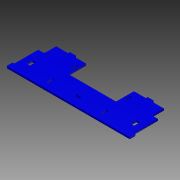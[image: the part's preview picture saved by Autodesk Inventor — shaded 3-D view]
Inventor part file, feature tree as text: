
AUTODESK INVENTOR PART (.ipt)
format: ipt  version: 2012 (Build 160160000, 160)  size: 176,640 bytes
history: native  units: mm
features: extrude x1, sketch x1
ambient origin geometry x8: Origin, YZ Plane, XZ Plane, XY Plane, X Axis, Y Axis, Z Axis, Center Point
feature tree (2):
  extrude  "Extrusion7"  Depth=30.0mm
  sketch  "Sketch1"  dims[d0=80.0mm d1=30.0mm d2=50.0mm d5=10.0mm d7=10.0mm d10=50.0mm d13=3.0mm d14=3.0mm d15=3.0mm d16=10.0mm d18=10.0mm d20=3.0mm d21=40.0mm d22=206.0mm d23=30.0mm d24=40.0mm d27=1.0mm d28=10.0mm d29=6.0mm d31=40.0mm d32=10.0mm d33=6.0mm d35=40.0mm d39=10.0mm d40=3.0mm d41=10.0mm d42=3.0mm d44=10.0mm d45=10.0mm d50=3.0mm d51=10.0mm d52=10.0mm d54=3.0mm d55=10.0mm d56=10.0mm d60=10.0mm d61=3.0mm d62=17.0mm d66=40.0mm d67=40.0mm d71=3.5mm d72=3.5mm d73=3.5mm d74=3.5mm d77=20.0mm d78=20.0mm d79=10.0mm d80=10.0mm d81=2.0mm d82=10.0mm d84=50.0mm d85=20.0mm d86=20.0mm d87=60.0mm d88=5.0mm d89=3.0mm d90=0.0mm d91=1.0mm]
